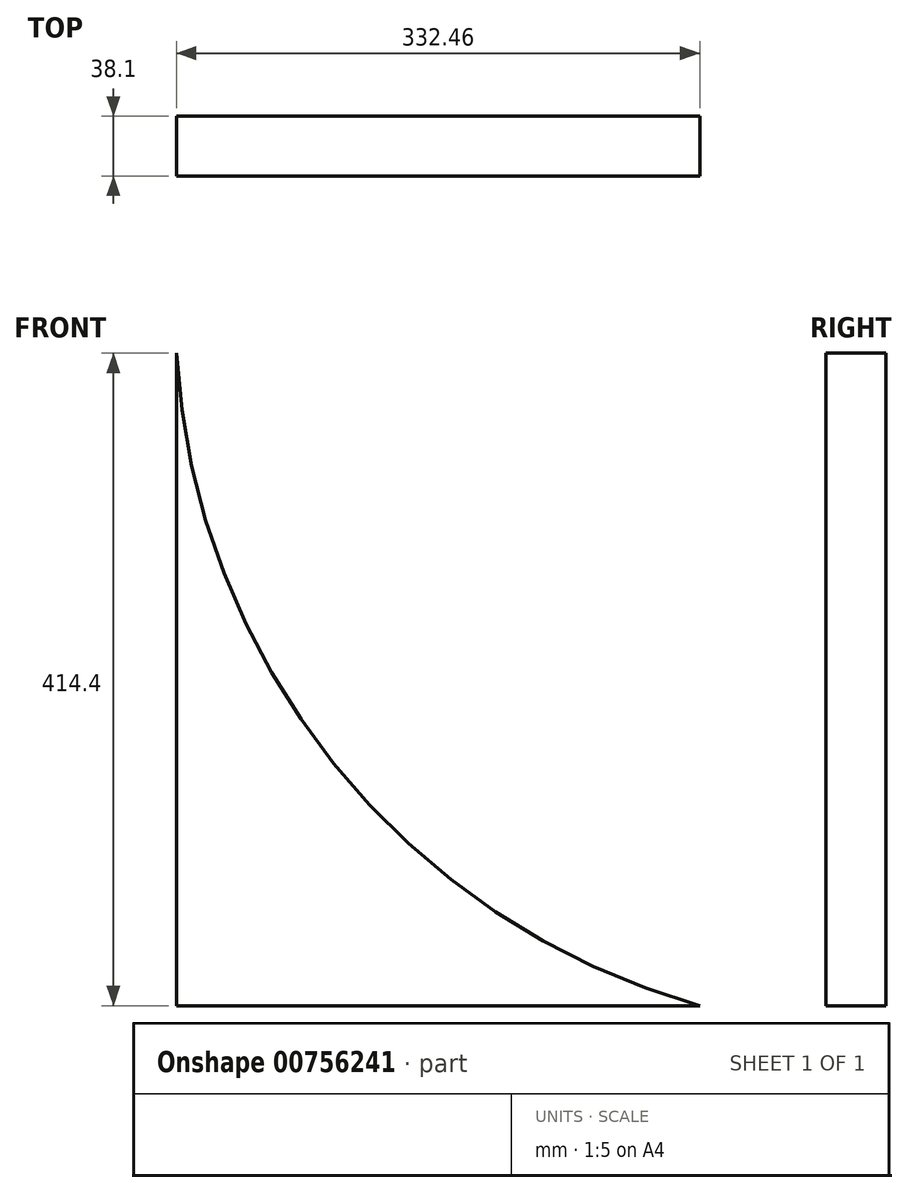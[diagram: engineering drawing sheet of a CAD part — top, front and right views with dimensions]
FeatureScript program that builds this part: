
annotation { "Feature Type Name" : "Feature", "Feature Type Description" : "" }
export const myFeature = defineFeature(function(context is Context, id is Id, definition is map)
    precondition{}
    {
        {
            var Q0;
            Q0=qCreatedBy(makeId("Front.planeOp"),FACE);
            var sketch = newSketch(context, id + "F0", { "sketchPlane" : qUnion([Q0])});
            skLineSegment(sketch, "E0.bottom", {"start": v(-1066.8, 609.6) * mm, "end": v(1066.8, 609.6) * mm});
            skLineSegment(sketch, "E0.top", {"start": v(-1066.8, -609.6) * mm, "end": v(1066.8, -609.6) * mm});
            skLineSegment(sketch, "E0.left", {"start": v(-1066.8, 609.6) * mm, "end": v(-1066.8, -609.6) * mm});
            skLineSegment(sketch, "E0.right", {"start": v(1066.8, 609.6) * mm, "end": v(1066.8, -609.6) * mm});
            skPoint(sketch, "E0.middle", {"position": v(0, 0) * mm});
            skArc(sketch, "E1", {"start": v(-1066.8, 66.97) * mm, "mid": v(-946.18, 479.4) * mm, "end": v(-536.67, 609.6) * mm});
            skArc(sketch, "E2", {"start": v(1066.8, 240.88) * mm, "mid": v(938.65, 483.9) * mm, "end": v(694.34, 609.6) * mm});
            skArc(sketch, "E3", {"start": v(-734.34, -609.6) * mm, "mid": v(-966.94, -455.64) * mm, "end": v(-1066.8, -195.2) * mm});
            skArc(sketch, "E4", {"start": v(658.1, -609.6) * mm, "mid": v(941.46, -470.12) * mm, "end": v(1066.8, -180.22) * mm});
            skLineSegment(sketch, "E5.bottom", {"start": v(-1066.8, 66.97) * mm, "end": v(-990.6, 66.97) * mm});
            skLineSegment(sketch, "E5.top", {"start": v(-1066.8, -25.4) * mm, "end": v(-990.6, -25.4) * mm});
            skLineSegment(sketch, "E5.left", {"start": v(-1066.8, 66.97) * mm, "end": v(-1066.8, -25.4) * mm});
            skLineSegment(sketch, "E5.right", {"start": v(-990.6, 66.97) * mm, "end": v(-990.6, -25.4) * mm});
            skLineSegment(sketch, "E6.bottom", {"start": v(1066.8, 66.97) * mm, "end": v(990.6, 66.97) * mm});
            skLineSegment(sketch, "E6.top", {"start": v(1066.8, -25.4) * mm, "end": v(990.6, -25.4) * mm});
            skLineSegment(sketch, "E6.left", {"start": v(1066.8, 66.97) * mm, "end": v(1066.8, -25.4) * mm});
            skLineSegment(sketch, "E6.right", {"start": v(990.6, 66.97) * mm, "end": v(990.6, -25.4) * mm});
            skSolve(sketch);
        }
        {
            var Q0;
            {var subQ10=sQuery(id+"F0.wireOp",EDGE,"E3");Q0=makeQuery(id+"F0.imprint","IMPRINT",FACE,{"disambiguationData":[TD([[makeQuery(id+"F0.imprint","IMPRINT",EDGE,{"derivedFrom":subQ10}),-1.0]])]});}
            extrude(context, id + "F1", {"entities" : qUnion([Q0]), "endBound" : BoundingType.SYMMETRIC, "depth" : 38.1 * mm, "offsetDistance" : 25.4 * mm});
        }
    });
